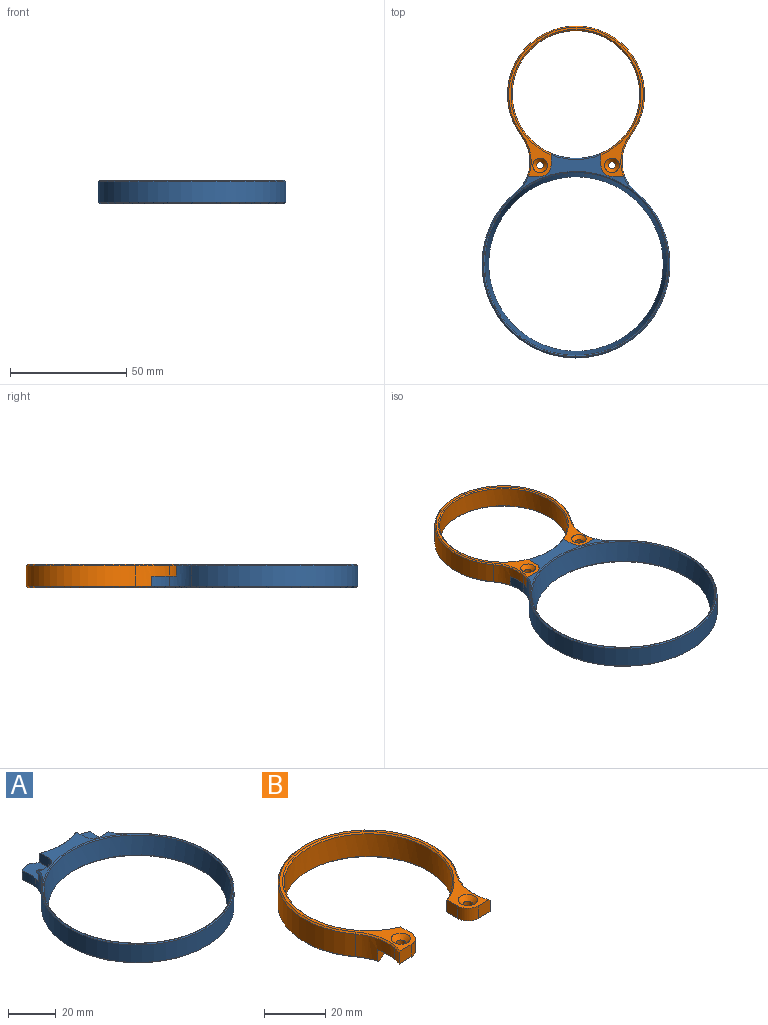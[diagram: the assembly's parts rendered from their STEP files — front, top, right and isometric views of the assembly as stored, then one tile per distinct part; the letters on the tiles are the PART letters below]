
ASSEMBLY  parts=2 mates=1
PART A: 47 faces, bbox 81x90.9x10 mm
  f0: cylinder r=1.55mm len=3.1mm, axis (0,0,1), area 26.3mm2, adj f4,f21
  f1: cylinder r=1.55mm len=3.1mm, axis (0,0,1), area 26.3mm2, adj f12,f28
  f2: plane 89.98x80mm, normal (0,0,-1), area 771mm2, adj f19,f20,f22,f23,f24,f25,f26,f27
  f3: cylinder r=27.53mm len=30.74mm, axis (0,0,-1), area 246.3mm2, adj f4,f12,f15,f16,f19,f20,f43,f44
  f4: plane 12.43x10.25mm, normal (0,0,1), area 93.9mm2, adj f0,f3,f6,f11,f16,f17,f18,f19
  f5: cylinder r=18.56mm len=7.59mm, axis (0,0,-1), area 34.4mm2, adj f7,f12,f20,f39
  f6: cylinder r=18.56mm len=7.59mm, axis (0,0,-1), area 34.4mm2, adj f4,f11,f19,f35
  f7: cylinder r=16mm len=9.51mm, axis (0,0,-1), area 87.1mm2, adj f5,f8,f12,f13,f38,f42
  f8: cylinder r=40.5mm len=81mm, axis (0,0,-1), area 1788.5mm2, adj f7,f11,f37,f41
  f9: plane 87.15x80mm, normal (0,0,1), area 195.8mm2, adj f13,f14,f15,f16,f17,f18,f40,f41
  f10: cone r=37.5mm half-angle=11.3deg, axis (0,0,1), area 2221.4mm2, adj f45,f46
  f11: cylinder r=16mm len=9.51mm, axis (0,0,-1), area 87.1mm2, adj f4,f6,f8,f18,f36,f40
  f12: plane 12.43x10.25mm, normal (0,0,1), area 93.9mm2, adj f1,f3,f5,f7,f13,f14,f15,f20
  f13: plane 5.51x5mm, normal (0,1,0), area 27.4mm2, adj f7,f9,f12,f14,f42
  f14: cylinder r=4.74mm len=5mm, axis (0,0,1), area 37.2mm2, adj f9,f12,f13,f15
  f15: plane 5.19x5mm, normal (-1,0,0), area 25.8mm2, adj f3,f9,f12,f14,f44
  f16: plane 5.19x5mm, normal (1,0,0), area 25.8mm2, adj f3,f4,f9,f17,f44
  f17: cylinder r=4.74mm len=5mm, axis (0,0,1), area 37.2mm2, adj f4,f9,f16,f18
  f18: plane 5.51x5mm, normal (0,1,0), area 27.4mm2, adj f4,f9,f11,f17,f40
  f19: plane 5x4.98mm, normal (0.34,0.94,0), area 26.2mm2, adj f2,f3,f4,f6,f35,f43
  f20: plane 5x4.98mm, normal (-0.34,0.94,0), area 26.2mm2, adj f2,f3,f5,f12,f39,f43
  f21: plane 6.34x5.71mm, normal (0,0,-1), area 18.6mm2, adj f0,f22,f23,f24,f25,f26,f27
  f22: plane 2.85x2.3mm, normal (-0.44,-0.9,0), area 7.3mm2, adj f2,f21,f23,f27
  f23: plane 3.17x2.3mm, normal (-1,-0.07,0), area 7.3mm2, adj f2,f21,f22,f24
  f24: plane 2.63x2.3mm, normal (-0.56,0.83,0), area 7.3mm2, adj f2,f21,f23,f25
  f25: plane 2.85x2.3mm, normal (0.44,0.9,0), area 7.3mm2, adj f2,f21,f24,f26
  f26: plane 3.17x2.3mm, normal (1,0.07,0), area 7.3mm2, adj f2,f21,f25,f27
  f27: plane 2.63x2.3mm, normal (0.56,-0.83,0), area 7.3mm2, adj f2,f21,f22,f26
  f28: plane 6.34x5.71mm, normal (0,0,-1), area 18.6mm2, adj f1,f29,f30,f31,f32,f33,f34
  f29: plane 2.85x2.3mm, normal (0.44,-0.9,0), area 7.3mm2, adj f2,f28,f30,f34
  f30: plane 2.63x2.3mm, normal (-0.56,-0.83,0), area 7.3mm2, adj f2,f28,f29,f31
  f31: plane 3.17x2.3mm, normal (-1,0.07,0), area 7.3mm2, adj f2,f28,f30,f32
  f32: plane 2.85x2.3mm, normal (-0.44,0.9,0), area 7.3mm2, adj f2,f28,f31,f33
  f33: plane 2.63x2.3mm, normal (0.56,0.83,0), area 7.3mm2, adj f2,f28,f32,f34
  f34: plane 3.17x2.3mm, normal (1,-0.07,0), area 7.3mm2, adj f2,f28,f29,f33
  f35: cone r=18.56mm half-angle=45deg, axis (0,0,-1), area 5.5mm2, adj f2,f6,f19,f36
  f36: cone r=16.5mm half-angle=45deg, axis (0,0,-1), area 8.1mm2, adj f2,f11,f35,f37
  f37: cone r=40.5mm half-angle=45deg, axis (0,0,1), area 139.6mm2, adj f2,f8,f36,f38
  f38: cone r=16.5mm half-angle=45deg, axis (0,0,-1), area 8.1mm2, adj f2,f7,f37,f39
  f39: cone r=19.06mm half-angle=45deg, axis (0,0,-1), area 5.5mm2, adj f2,f5,f20,f38
  f40: cone r=16.5mm half-angle=45deg, axis (0,0,1), area 5.9mm2, adj f9,f11,f18,f41
  f41: cone r=40mm half-angle=45deg, axis (0,0,-1), area 139.6mm2, adj f8,f9,f40,f42
  f42: cone r=16.5mm half-angle=45deg, axis (0,0,1), area 5.9mm2, adj f7,f9,f13,f41
  f43: cone r=28.03mm half-angle=45deg, axis (0,0,-1), area 23.5mm2, adj f2,f3,f19,f20
  f44: cone r=27.53mm half-angle=45deg, axis (0,0,1), area 15.6mm2, adj f3,f9,f15,f16
  f45: cone r=39.91mm half-angle=50.7deg, axis (0,0,1), area 158mm2, adj f9,f10
  f46: cone r=38.11mm half-angle=39.3deg, axis (0,0,-1), area 184mm2, adj f2,f10
PART B: 32 faces, bbox 59.1x65x10 mm
  f0: plane 12.43x10.25mm, normal (0,0,-1), area 93.9mm2, adj f1,f4,f6,f8,f14,f15,f16,f18
  f1: cylinder r=27.53mm len=55.07mm, axis (0,0,-1), area 1310.8mm2, adj f0,f10,f11,f14,f17,f18,f30,f31
  f2: plane 64.31x58.07mm, normal (0,0,1), area 283.2mm2, adj f11,f12,f13,f14,f15,f16,f20,f21
  f3: cylinder r=16mm len=4.5mm, axis (0,0,-1), area 14.2mm2, adj f5,f10,f13,f25
  f4: cylinder r=16mm len=4.5mm, axis (0,0,-1), area 14.2mm2, adj f0,f6,f15,f29
  f5: cylinder r=18.56mm len=14.47mm, axis (0,0,-1), area 103.3mm2, adj f3,f7,f10,f17,f22,f26
  f6: cylinder r=18.56mm len=14.47mm, axis (0,0,-1), area 103.3mm2, adj f0,f4,f7,f18,f24,f28
  f7: cylinder r=29.53mm len=59.07mm, axis (0,0,-1), area 1178.4mm2, adj f5,f6,f23,f27
  f8: cylinder r=1.55mm len=3.4mm, axis (0,0,1), area 33.1mm2, adj f0,f20
  f9: cylinder r=1.55mm len=3.4mm, axis (0,0,1), area 33.1mm2, adj f10,f21
  f10: plane 12.43x10.25mm, normal (0,0,-1), area 93.9mm2, adj f1,f3,f5,f9,f11,f12,f13,f17
  f11: plane 5.19x5mm, normal (1,0,0), area 25.8mm2, adj f1,f2,f10,f12,f31
  f12: cylinder r=4.74mm len=5mm, axis (0,0,-1), area 37.2mm2, adj f2,f10,f11,f13
  f13: plane 5.51x5mm, normal (0,-1,0), area 27.4mm2, adj f2,f3,f10,f12,f25
  f14: plane 5.19x5mm, normal (-1,0,0), area 25.8mm2, adj f0,f1,f2,f16,f31
  f15: plane 5.51x5mm, normal (0,-1,0), area 27.4mm2, adj f0,f2,f4,f16,f29
  f16: cylinder r=4.74mm len=5mm, axis (0,0,-1), area 37.2mm2, adj f0,f2,f14,f15
  f17: plane 5x4.98mm, normal (0.34,-0.94,0), area 26.2mm2, adj f1,f5,f10,f19,f22,f30
  f18: plane 5x4.98mm, normal (-0.34,-0.94,0), area 26.2mm2, adj f0,f1,f6,f19,f24,f30
  f19: plane 58.07x53.51mm, normal (0,0,-1), area 159.2mm2, adj f17,f18,f22,f23,f24,f30
  f20: cone r=1.55mm half-angle=45deg, axis (0,0,1), area 33.4mm2, adj f2,f8
  f21: cone r=1.55mm half-angle=45deg, axis (0,0,1), area 33.4mm2, adj f2,f9
  f22: cone r=19.06mm half-angle=45deg, axis (0,0,-1), area 5.5mm2, adj f5,f17,f19,f23
  f23: cone r=29.03mm half-angle=45deg, axis (0,0,1), area 91.8mm2, adj f7,f19,f22,f24
  f24: cone r=18.56mm half-angle=45deg, axis (0,0,-1), area 5.5mm2, adj f6,f18,f19,f23
  f25: cone r=16.5mm half-angle=45deg, axis (0,0,1), area 2.2mm2, adj f2,f3,f13,f26
  f26: cone r=18.56mm half-angle=45deg, axis (0,0,1), area 11mm2, adj f2,f5,f25,f27
  f27: cone r=29.03mm half-angle=45deg, axis (0,0,-1), area 91.8mm2, adj f2,f7,f26,f28
  f28: cone r=19.06mm half-angle=45deg, axis (0,0,1), area 11mm2, adj f2,f6,f27,f29
  f29: cone r=16.5mm half-angle=45deg, axis (0,0,1), area 2.2mm2, adj f2,f4,f15,f28
  f30: cone r=27.53mm half-angle=45deg, axis (0,0,-1), area 99.9mm2, adj f1,f17,f18,f19
  f31: cone r=27.53mm half-angle=45deg, axis (0,0,1), area 107.8mm2, adj f1,f2,f11,f14
PLACE A t=(0,73.03,0)mm
PLACE B t=(0,73.03,0)mm
MATE fastened A.f1 <-> B.f9  axis (0,0,1) through (-15.5,42.5,5)mm
